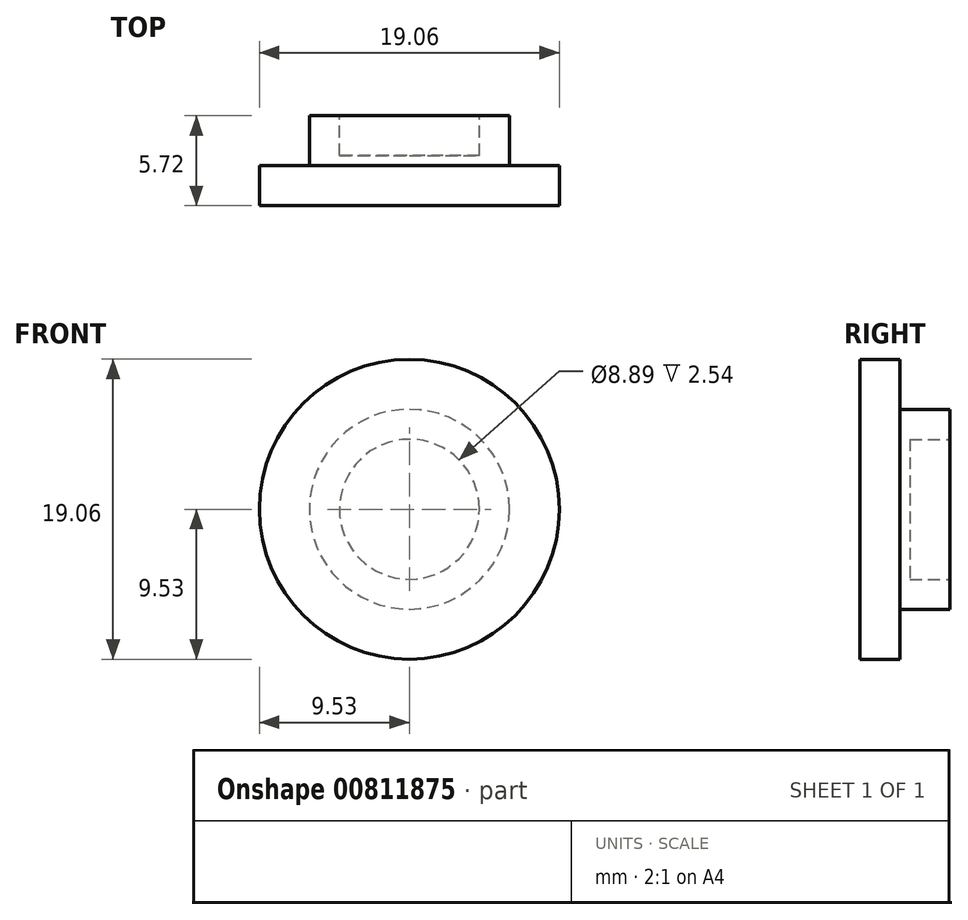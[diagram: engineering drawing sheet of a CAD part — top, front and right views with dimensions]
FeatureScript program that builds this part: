
annotation { "Feature Type Name" : "Feature", "Feature Type Description" : "" }
export const myFeature = defineFeature(function(context is Context, id is Id, definition is map)
    precondition{}
    {
        {
            var Q0;
            Q0=qCreatedBy(makeId("Front.planeOp"),FACE);
            var sketch = newSketch(context, id + "F0", { "sketchPlane" : qUnion([Q0])});
            skCircle(sketch, "E0", {"center": v(0, 0) * mm, "radius": 6.35 * mm});
            skSolve(sketch);
        }
        {
            var Q0;
            Q0 = qSketchRegion(id + "F0", true);
            extrude(context, id + "F1", {"entities" : qUnion([Q0]), "depth" : 3.17 * mm, "offsetDistance" : 25.4 * mm});
        }
        {
            var Q0;
            Q0=makeQuery(id+"F1.opExtrude","CAP_FACE",FACE,{"disambiguationData":[OSD([sQuery(id+"F0.wireOp",EDGE,"E0")])],"isStart":false});
            var sketch = newSketch(context, id + "F2", { "sketchPlane" : qUnion([Q0])});
            skCircle(sketch, "E1", {"center": v(0, 0) * mm, "radius": 9.53 * mm});
            skSolve(sketch);
        }
        {
            var Q0;
            Q0=makeQuery(id+"F2.imprint","IMPRINT",FACE,{"disambiguationData":[TD([[makeQuery(id+"F2.imprint","IMPRINT",EDGE,{"derivedFrom":sQuery(id+"F2.wireOp",EDGE,"E1")}),1.0]])]});
            var Q1;
            Q1=makeQuery(id+"F2.imprint","IMPRINT",FACE,{"disambiguationData":[TD([[makeQuery(id+"F2.imprint","IMPRINT",EDGE,{"derivedFrom":makeQuery(id+"F1.opExtrude","CAP_EDGE",EDGE,{"disambiguationData":[OSD([sQuery(id+"F0.wireOp",EDGE,"E0")])],"isStart":false})}),1.0]])]});
            extrude(context, id + "F3", {"entities" : qUnion([Q0, Q1]), "operationType" : NewBodyOperationType.ADD, "depth" : 2.54 * mm, "offsetDistance" : 25.4 * mm});
        }
        {
            var Q0;
            Q0=makeQuery(id+"F1.opExtrude","CAP_FACE",FACE,{"disambiguationData":[OSD([sQuery(id+"F0.wireOp",EDGE,"E0")])],"isStart":true});
            var sketch = newSketch(context, id + "F4", { "sketchPlane" : qUnion([Q0])});
            skCircle(sketch, "E2", {"center": v(0, 0) * mm, "radius": 4.45 * mm});
            skSolve(sketch);
        }
        {
            var Q0;
            Q0=makeQuery(id+"F4.imprint","IMPRINT",FACE,{"disambiguationData":[TD([[makeQuery(id+"F4.imprint","IMPRINT",EDGE,{"derivedFrom":sQuery(id+"F4.wireOp",EDGE,"E2")}),1.0]])]});
            extrude(context, id + "F5", {"entities" : qUnion([Q0]), "operationType" : NewBodyOperationType.REMOVE, "oppositeDirection" : true, "depth" : 2.54 * mm, "offsetDistance" : 25.4 * mm});
        }
    });
